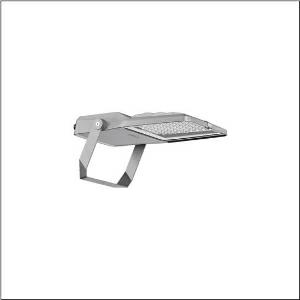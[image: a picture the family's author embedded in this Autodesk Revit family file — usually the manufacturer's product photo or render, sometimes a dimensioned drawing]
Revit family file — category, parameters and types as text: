
# Revit family: floodlight_fl_21_mini___pl33t_5xa7776b2f1a_8d7b
name_source: partatom
category: Lighting Fixtures
units: mm (PartAtom-declared; Revit-internal decimal feet)

## family parameters
Cut with Voids When Loaded = No
Host = Face
Light Source = No
Part Type = Normal
Room Calculation Point = No
Round Connector Dimension = Use Diameter
Shared = No

## types (1)
- --- (1 x LED, 6150 lm, 45.7 W, 3000K)
    Apparent Load = 46 VA
    CIE Flux Codes = 26 75 99 100 100
    Color Rendering = 70
    Color Temperature = 3000K
    Default Elevation = 1800 mm
    Description = Floodlight FL 21 mini, floodlight, primary light control with lens, of PMMA, primary optical cover: protective disc, of toughened safety glass, transparent, light distribution: PL33T, light emission: direct distribution, installation type: surface-mounted, LED, High Power LED, rated luminous flux: 6.150lm, luminous efficacy: 135lm/W, light colour: 730, colour temperature: 3000K, control gear: Smart Interface (Zhaga), control: flexible luminous flux parameterisation, time-dependent luminous flux control, constant luminous flux control, overheat protection, pre-setting: logarithmic dimming characteristic, with terminal, 6-pole, mains connection: 220..240V, AC, 50/60Hz, start of lifetime: 46W, end of service life: 48W, reduction: 22W, luminaire housing, of diecast aluminium, powder-coated, Siteco® metallic grey (DB 702S), corrosivity category C5 mid according to DIN EN ISO 12944, suitable for swimming pools, chlorine-resistant, sealing non-destructively replaceable, mounting bracket, of steel, galvanised, powder-coated, Siteco® metallic grey (DB 702S), Smart Interface below and above, protection rating (complete): IP66, insulation class (complete): insulation class II (safety insulation), certification: CE, ENEC, VDE, protection symbol: D, impact resistance: IK08, permissible operating ambient temperature: -40..+40°C, permissible operating ambient temperature for outdoor applications: -40..+50°C, standard: DIN EN 12944, LABS conformity tested according to VDMA 24364:2018-05, packaging unit: 1 piece

Light Distribution: PL33T
    Height = 70 mm
    Lamp = 1 x LED
    Lamp Light Flux = 6150 lm
    Lamp Power = 45.7 W
    Lamp count = 1
    Length = 485 mm
    Luminous efficacy = 135 lm/W
    Manufacturer = Siteco
    ModVariant = No
    Model = 5XA7776B2F1A
    Number of Poles = 1
    OnlyDefault = Yes
    Power Factor = 1
    Product Name = Floodlight FL 21 mini | PL33T
    Product group = floodlight | pylon annexe
    ProductGroupID = 6200
    Protection Class = Protection class II
    Protection Degree = IP 66
    RLX_Detail_Level = 1
    RLX_Emergency_Light_Flux = 0 lm
    RLX_Emergency_Type = 0
    RLX_Emergency_Type_DB = No
    RlxData = <blob elided: 96033 chars, md5=9ea3add6>
    Socket = socket
    Standby Power = 0 W
    System Light Flux = 6150 lm
    System Power = 46 W
    Type Comments = factory setting: luminous flux: 100 % | dim-lin: 254 | 463 mA
    Type Image = l_1006845.jpg
    URL = http://relux.com
    VarID = @adj_148640
    Voltage = 0 V
    Weight = 0.00 kg
    Width = 337 mm

## geometry (parser evidence)
native form markers: Blend x4, Sweep x10
no freeform markers — native parametric forms only
